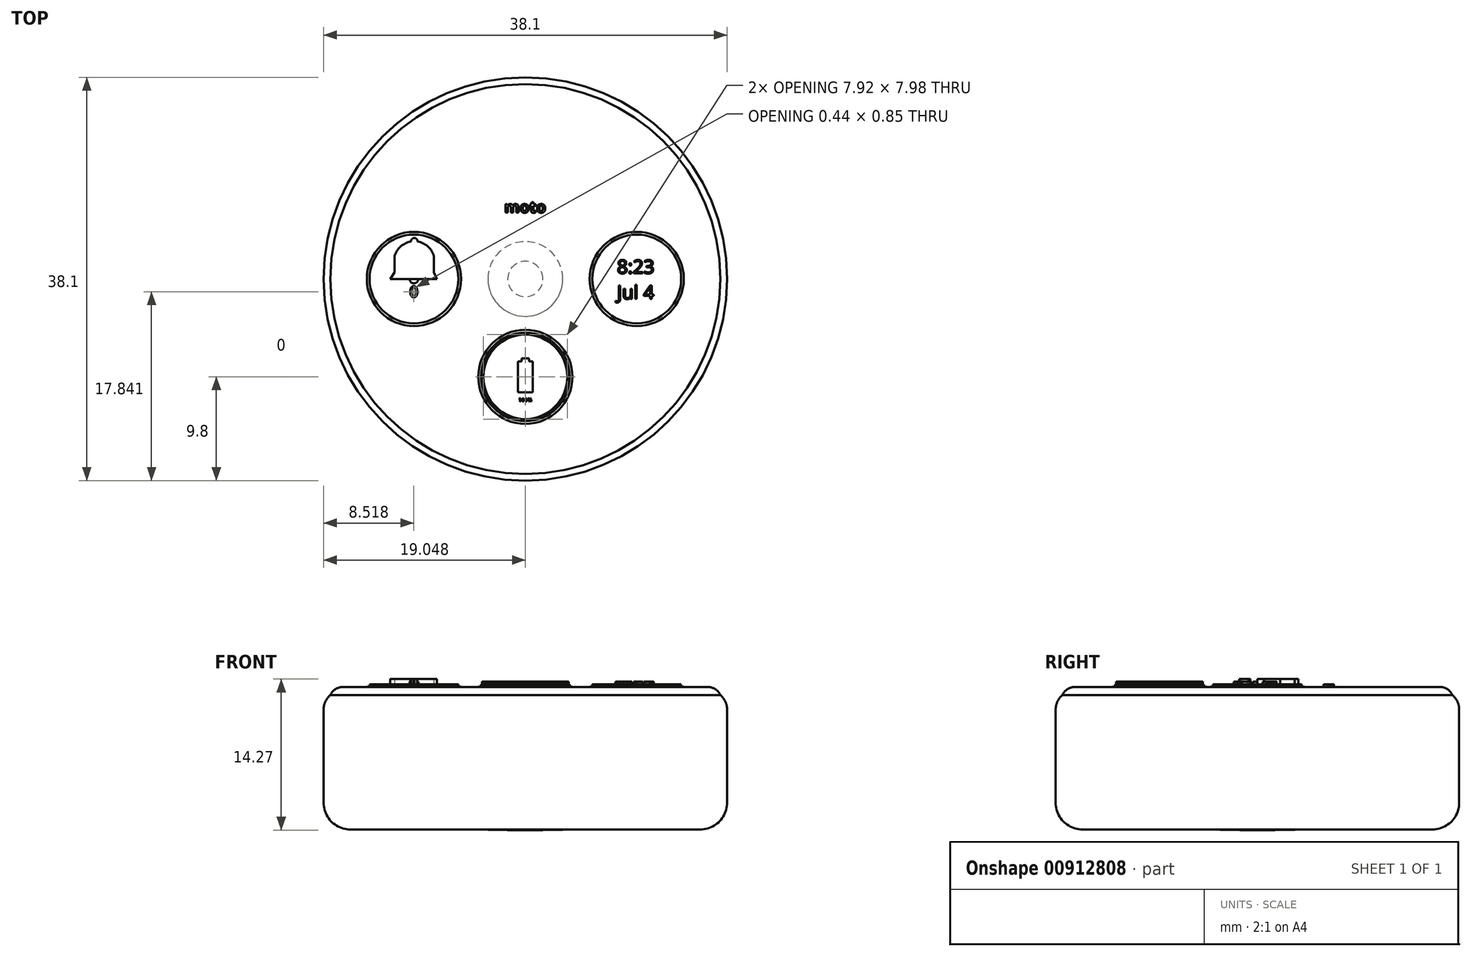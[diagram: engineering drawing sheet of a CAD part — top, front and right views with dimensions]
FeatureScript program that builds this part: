
annotation { "Feature Type Name" : "Feature", "Feature Type Description" : "" }
export const myFeature = defineFeature(function(context is Context, id is Id, definition is map)
    precondition{}
    {
        {
            var Q0;
            Q0=qCreatedBy(makeId("Top.planeOp"),FACE);
            var sketch = newSketch(context, id + "F0", { "sketchPlane" : qUnion([Q0])});
            skCircle(sketch, "E0", {"center": v(0, 0) * mm, "radius": 19.05 * mm});
            skSolve(sketch);
        }
        {
            var Q0;
            Q0 = qSketchRegion(id + "F0", true);
            extrude(context, id + "F1", {"entities" : qUnion([Q0]), "depth" : 12.7 * mm, "offsetDistance" : 25.4 * mm});
        }
        {
            var Q0;
            Q0=makeQuery(id+"F1.opExtrude","CAP_FACE",FACE,{"disambiguationData":[OSD([sQuery(id+"F0.wireOp",EDGE,"E0")])],"isStart":false});
            var sketch = newSketch(context, id + "F2", { "sketchPlane" : qUnion([Q0])});
            skCircle(sketch, "E1", {"center": v(0, 0) * mm, "radius": 18.41 * mm});
            skSolve(sketch);
        }
        {
            var Q0;
            Q0 = qSketchRegion(id + "F2", true);
            extrude(context, id + "F3", {"entities" : qUnion([Q0]), "operationType" : NewBodyOperationType.ADD, "depth" : 0.76 * mm, "offsetDistance" : 25.4 * mm});
        }
        {
            var Q0;
            Q0=makeQuery(id+"F3.opExtrude","CAP_EDGE",EDGE,{"disambiguationData":[OSD([sQuery(id+"F2.wireOp",EDGE,"E1")])],"isStart":false});
            fillet(context, id + "F4", {"entities" : qUnion([Q0]), "radius" : 1.27 * mm, "tangentPropagation" : true, "allowEdgeOverflow" : false});
        }
        {
            var Q0;
            Q0=makeQuery(id+"F1.opExtrude","CAP_EDGE",EDGE,{"disambiguationData":[OSD([sQuery(id+"F0.wireOp",EDGE,"E0")])],"isStart":false});
            fillet(context, id + "F5", {"entities" : qUnion([Q0]), "radius" : 1.78 * mm, "tangentPropagation" : true, "allowEdgeOverflow" : false});
        }
        {
            var Q0;
            Q0=makeQuery(id+"F1.opExtrude","CAP_EDGE",EDGE,{"disambiguationData":[OSD([sQuery(id+"F0.wireOp",EDGE,"E0")])],"isStart":true});
            fillet(context, id + "F6", {"entities" : qUnion([Q0]), "radius" : 2.54 * mm, "tangentPropagation" : true, "allowEdgeOverflow" : false});
        }
        {
            var Q0;
            Q0=makeQuery(id+"F1.opExtrude","CAP_FACE",FACE,{"disambiguationData":[OSD([sQuery(id+"F0.wireOp",EDGE,"E0")])],"isStart":true});
            var sketch = newSketch(context, id + "F7", { "sketchPlane" : qUnion([Q0])});
            skCircle(sketch, "E2", {"center": v(0, 0) * mm, "radius": 3.53 * mm});
            skCircle(sketch, "E3", {"center": v(0, 0) * mm, "radius": 1.66 * mm});
            skSolve(sketch);
        }
        {
            var Q0;
            Q0 = qSketchRegion(id + "F7", true);
            extrude(context, id + "F8", {"entities" : qUnion([Q0]), "operationType" : NewBodyOperationType.ADD, "depth" : 0.03 * mm, "offsetDistance" : 25.4 * mm});
        }
        {
            var Q0;
            Q0=makeQuery(id+"F8.boolean.opBoolean","SPLIT",FACE,{"disambiguationData":[TD([makeQuery(id+"F8.opExtrude","SWEPT_FACE",FACE,{"disambiguationData":[OSD([sQuery(id+"F7.wireOp",EDGE,"E3")])]})])],"derivedFrom":makeQuery(id+"F1.opExtrude","CAP_FACE",FACE,{"disambiguationData":[OSD([sQuery(id+"F0.wireOp",EDGE,"E0")])],"isStart":true})});
            extrude(context, id + "F9", {"entities" : qUnion([Q0]), "operationType" : NewBodyOperationType.ADD, "depth" : 0.05 * mm, "offsetDistance" : 25.4 * mm});
        }
        {
            var Q0;
            Q0=makeQuery(id+"F3.opExtrude","CAP_FACE",FACE,{"disambiguationData":[OSD([sQuery(id+"F2.wireOp",EDGE,"E1")])],"isStart":false});
            var sketch = newSketch(context, id + "F10", { "sketchPlane" : qUnion([Q0])});
            skText(sketch, "E4", { "text": "moto", "fontName": "OpenSans-Bold.ttf"});
            skCircle(sketch, "E5", {"center": v(0, -9.25) * mm, "radius": 4.2 * mm});
            skCircle(sketch, "E6", {"center": v(10.52, 0) * mm, "radius": 4.2 * mm});
            skCircle(sketch, "E7", {"center": v(-10.52, 0) * mm, "radius": 4.2 * mm});
            const initialGuessF10  = {"E4": [-0.00199, 0.00626, 1, 0, 0.00107]};
            skSetInitialGuess(sketch, initialGuessF10);
            skSolve(sketch);
        }
        {
            var Q0;
            Q0 = qSketchRegion(id + "F10", true);
            extrude(context, id + "F11", {"entities" : qUnion([Q0]), "operationType" : NewBodyOperationType.ADD, "depth" : 0.25 * mm, "offsetDistance" : 25.4 * mm});
        }
        {
            var Q0;
            {var subQ0=sQuery(id+"F2.wireOp",EDGE,"E1");Q0=makeQuery(id+"F11.boolean.opBoolean","SPLIT",FACE,{"disambiguationData":[TD([makeQuery(id+"F4.opFillet","BLEND_FACE",FACE,{"disambiguationData":[OSD([subQ0])]})])],"derivedFrom":makeQuery(id+"F3.opExtrude","CAP_FACE",FACE,{"disambiguationData":[OSD([subQ0])],"isStart":false})});}
            var sketch = newSketch(context, id + "F12", { "sketchPlane" : qUnion([Q0])});
            skCircle(sketch, "E8", {"center": v(-10.52, 0) * mm, "radius": 4.45 * mm});
            skCircle(sketch, "E9", {"center": v(0, -9.25) * mm, "radius": 4.45 * mm});
            skCircle(sketch, "E10", {"center": v(10.52, 0) * mm, "radius": 4.45 * mm});
            skSolve(sketch);
        }
        {
            var Q0;
            Q0 = qSketchRegion(id + "F12", true);
            extrude(context, id + "F13", {"entities" : qUnion([Q0]), "operationType" : NewBodyOperationType.ADD, "depth" : 0.03 * mm, "offsetDistance" : 25.4 * mm});
        }
        {
            var Q0;
            Q0=makeQuery(id+"F11.opExtrude","CAP_FACE",FACE,{"disambiguationData":[OSD([sQuery(id+"F10.wireOp",EDGE,"E5")])],"isStart":false});
            var sketch = newSketch(context, id + "F14", { "sketchPlane" : qUnion([Q0])});
            skLineSegment(sketch, "E11.top", {"start": v(-0.69, -10.72) * mm, "end": v(0.69, -10.72) * mm});
            skLineSegment(sketch, "E11.left", {"start": v(-0.69, -7.78) * mm, "end": v(-0.69, -10.72) * mm});
            skLineSegment(sketch, "E11.right", {"start": v(0.69, -7.78) * mm, "end": v(0.69, -10.72) * mm});
            skPoint(sketch, "E11.middle", {"position": v(0, -9.25) * mm});
            skLineSegment(sketch, "E12.bottom", {"start": v(-0.35, -7.52) * mm, "end": v(0.35, -7.52) * mm});
            skPoint(sketch, "E12.middle", {"position": v(0, -7.78) * mm});
            skLineSegment(sketch, "E13", {"start": v(-0.35, -7.52) * mm, "end": v(-0.35, -7.78) * mm});
            skLineSegment(sketch, "E14", {"start": v(0.35, -7.52) * mm, "end": v(0.35, -7.78) * mm});
            skLineSegment(sketch, "E15", {"start": v(-0.69, -7.78) * mm, "end": v(-0.35, -7.78) * mm});
            skLineSegment(sketch, "E16", {"start": v(0.69, -7.78) * mm, "end": v(0.35, -7.78) * mm});
            skPoint(sketch, "E17.startSnap0", {"position": v(0, -7.52) * mm});
            skPoint(sketch, "E17.endSnap0", {"position": v(0, -7.52) * mm});
            skPoint(sketch, "E18", {"position": v(0, -5.26) * mm});
            skPoint(sketch, "E19", {"position": v(0, -13.24) * mm});
            skArc(sketch, "E20", {"start": v(0, -13.24) * mm, "mid": v(3.96, -9.25) * mm, "end": v(0, -5.26) * mm});
            skArc(sketch, "E21", {"start": v(0, -5.26) * mm, "mid": v(-3.96, -9.25) * mm, "end": v(0, -13.24) * mm});
            skPoint(sketch, "E22", {"position": v(0, -5.16) * mm});
            skPoint(sketch, "E23", {"position": v(0, -13.34) * mm});
            skArc(sketch, "E24", {"start": v(0, -13.34) * mm, "mid": v(4.09, -9.25) * mm, "end": v(0, -5.16) * mm});
            skArc(sketch, "E25", {"start": v(0, -5.16) * mm, "mid": v(-4.08, -9.25) * mm, "end": v(0, -13.34) * mm});
            skText(sketch, "E26", { "text": "100%\n", "fontName": "OpenSans-Regular.ttf"});
            const initialGuessF14  = {"E26": [-0.00064, -0.0116, 1, 0, 0.00036]};
            skSetInitialGuess(sketch, initialGuessF14);
            skSolve(sketch);
        }
        {
            var Q0;
            {var subQ4=sQuery(id+"F14.wireOp",EDGE,"E11.left");Q0=makeQuery(id+"F14.imprint","IMPRINT",FACE,{"disambiguationData":[TD([[makeQuery(id+"F14.imprint","IMPRINT",EDGE,{"derivedFrom":subQ4}),1.0]])]});}
            var Q1;
            {var subQ4=sQuery(id+"F14.wireOp",EDGE,"E11.right");Q1=makeQuery(id+"F14.imprint","IMPRINT",FACE,{"disambiguationData":[TD([[makeQuery(id+"F14.imprint","IMPRINT",EDGE,{"derivedFrom":subQ4}),-1.0]])]});}
            extrude(context, id + "F15", {"entities" : qUnion([Q0, Q1]), "depth" : 0.03 * mm, "offsetDistance" : 25.4 * mm});
        }
        {
            var Q0;
            {var subQ0=sQuery(id+"F14.wireOp",EDGE,"E21");Q0=makeQuery(id+"F14.imprint","IMPRINT",FACE,{"disambiguationData":[TD([[makeQuery(id+"F14.imprint","IMPRINT",EDGE,{"derivedFrom":subQ0}),-1.0]])]});}
            var Q1;
            {var subQ1=sQuery(id+"F14.wireOp",EDGE,"E20");Q1=makeQuery(id+"F14.imprint","IMPRINT",FACE,{"disambiguationData":[TD([[makeQuery(id+"F14.imprint","IMPRINT",EDGE,{"derivedFrom":subQ1}),-1.0]])]});}
            var Q2;
            Q2=sQuery(id+"F14.wireOp",EDGE,"E25");
            var Q3;
            Q3=sQuery(id+"F14.wireOp",EDGE,"E24");
            extrude(context, id + "F16", {"entities" : qUnion([Q0, Q1]), "surfaceEntities" : qUnion([Q2, Q3]), "depth" : 0.03 * mm, "offsetDistance" : 25.4 * mm});
        }
        {
            var Q0;
            Q0 = qSketchRegion(id + "F14", true);
            extrude(context, id + "F17", {"entities" : qUnion([Q0]), "depth" : 0.25 * mm, "offsetDistance" : 25.4 * mm});
        }
        {
            var Q0;
            Q0=makeQuery(id+"F14.imprint","IMPRINT",FACE,{"disambiguationData":[TD([[makeQuery(id+"F14.imprint","IMPRINT",EDGE,{"derivedFrom":sQuery(id+"F14.wireOp",EDGE,"E26.sketch_text.stroke-33")}),1.0]])]});
            var Q1;
            Q1=makeQuery(id+"F14.imprint","IMPRINT",FACE,{"disambiguationData":[TD([[makeQuery(id+"F14.imprint","IMPRINT",EDGE,{"derivedFrom":sQuery(id+"F14.wireOp",EDGE,"E26.sketch_text.stroke-17")}),1.0]])]});
            var Q2;
            Q2=makeQuery(id+"F14.imprint","IMPRINT",FACE,{"disambiguationData":[TD([[makeQuery(id+"F14.imprint","IMPRINT",EDGE,{"derivedFrom":sQuery(id+"F14.wireOp",EDGE,"E26.sketch_text.stroke-0")}),-1.0]])]});
            var Q3;
            Q3=makeQuery(id+"F14.imprint","IMPRINT",FACE,{"disambiguationData":[TD([[makeQuery(id+"F14.imprint","IMPRINT",EDGE,{"derivedFrom":sQuery(id+"F14.wireOp",EDGE,"E26.sketch_text.stroke-41")}),1.0]])]});
            var Q4;
            Q4=makeQuery(id+"F14.imprint","IMPRINT",FACE,{"disambiguationData":[TD([[makeQuery(id+"F14.imprint","IMPRINT",EDGE,{"derivedFrom":sQuery(id+"F14.wireOp",EDGE,"E26.sketch_text.stroke-71")}),-1.0]])]});
            var Q5;
            Q5=makeQuery(id+"F14.imprint","IMPRINT",FACE,{"disambiguationData":[TD([[makeQuery(id+"F14.imprint","IMPRINT",EDGE,{"derivedFrom":sQuery(id+"F14.wireOp",EDGE,"E26.sketch_text.stroke-55")}),1.0]])]});
            extrude(context, id + "F18", {"entities" : qUnion([Q0, Q1, Q2, Q3, Q4, Q5]), "operationType" : NewBodyOperationType.ADD, "depth" : 0.25 * mm, "offsetDistance" : 25.4 * mm});
        }
        {
            var Q0;
            {var subQ0=sQuery(id+"F2.wireOp",EDGE,"E1");Q0=makeQuery(id+"F11.boolean.opBoolean","SPLIT",FACE,{"disambiguationData":[TD([makeQuery(id+"F4.opFillet","BLEND_FACE",FACE,{"disambiguationData":[OSD([subQ0])]})])],"derivedFrom":makeQuery(id+"F3.opExtrude","CAP_FACE",FACE,{"disambiguationData":[OSD([subQ0])],"isStart":false})});}
            var sketch = newSketch(context, id + "F19", { "sketchPlane" : qUnion([Q0])});
            skLineSegment(sketch, "E27.bottom", {"start": v(0, 14.95) * mm, "end": v(0, 14.95) * mm});
            skLineSegment(sketch, "E27.top", {"start": v(0, 0) * mm, "end": v(0, 0) * mm});
            skLineSegment(sketch, "E27.left", {"start": v(0, 14.95) * mm, "end": v(0, 0) * mm});
            skLineSegment(sketch, "E27.right", {"start": v(0, 14.95) * mm, "end": v(0, 0) * mm});
            skPoint(sketch, "E27.middle", {"position": v(0, 7.47) * mm});
            skPoint(sketch, "E28", {"position": v(0, 0) * mm});
            skLineSegment(sketch, "E29", {"start": v(0, 0) * mm, "end": v(4.6, 0) * mm});
            skLineSegment(sketch, "E30", {"start": v(4.6, 0) * mm, "end": v(4.6, 0) * mm});
            skLineSegment(sketch, "E31", {"start": v(4.6, 0) * mm, "end": v(0, 0) * mm});
            skSolve(sketch);
        }
        {
            var Q0;
            Q0=sQuery(id+"F19.wireOp",EDGE,"E27.right");
            var Q1;
            Q1=sQuery(id+"F19.wireOp",EDGE,"E31");
            extrude(context, id + "F20", {"bodyType" : ToolBodyType.SURFACE, "surfaceEntities" : qUnion([Q0, Q1]), "depth" : 0.25 * mm, "offsetDistance" : 25.4 * mm});
        }
        {
            var Q0;
            Q0=makeQuery(id+"F11.opExtrude","CAP_FACE",FACE,{"disambiguationData":[OSD([sQuery(id+"F10.wireOp",EDGE,"E6")])],"isStart":false});
            var sketch = newSketch(context, id + "F21", { "sketchPlane" : qUnion([Q0])});
            skText(sketch, "E32", { "text": "8:23\nJul 4", "fontName": "OpenSans-Regular.ttf"});
            const initialGuessF21  = {"E32": [0.00866, 0.00052, 1, 0, 0.00128]};
            skSetInitialGuess(sketch, initialGuessF21);
            skSolve(sketch);
        }
        {
            var Q0;
            Q0 = qSketchRegion(id + "F21", true);
            extrude(context, id + "F22", {"entities" : qUnion([Q0]), "depth" : 0.25 * mm, "offsetDistance" : 25.4 * mm});
        }
        {
            var Q0;
            Q0=makeQuery(id+"F11.opExtrude","CAP_FACE",FACE,{"disambiguationData":[OSD([sQuery(id+"F10.wireOp",EDGE,"E7")])],"isStart":false});
            var sketch = newSketch(context, id + "F23", { "sketchPlane" : qUnion([Q0])});
            skLineSegment(sketch, "E33", {"start": v(-10.52, 0) * mm, "end": v(-12.75, 0) * mm});
            skLineSegment(sketch, "E34", {"start": v(-10.52, 0) * mm, "end": v(-8.35, 0) * mm});
            skLineSegment(sketch, "E35", {"start": v(-8.35, 0) * mm, "end": v(-8.62, 0.63) * mm});
            skLineSegment(sketch, "E36", {"start": v(-8.62, 0.63) * mm, "end": v(-12.35, 0.63) * mm});
            skLineSegment(sketch, "E37", {"start": v(-12.35, 0.63) * mm, "end": v(-12.75, 0) * mm});
            skLineSegment(sketch, "E38", {"start": v(-12.35, 0.63) * mm, "end": v(-12.35, 2.15) * mm});
            skLineSegment(sketch, "E39", {"start": v(-8.62, 0.63) * mm, "end": v(-8.62, 2.15) * mm});
            skLineSegment(sketch, "E40", {"start": v(-12.35, 2.15) * mm, "end": v(-8.62, 2.15) * mm});
            skArc(sketch, "E41", {"start": v(-8.62, 2.15) * mm, "mid": v(-10.49, 3.56) * mm, "end": v(-12.35, 2.15) * mm});
            skArc(sketch, "E42", {"start": v(-10.18, 3.53) * mm, "mid": v(-10.49, 3.87) * mm, "end": v(-10.8, 3.53) * mm});
            skArc(sketch, "E43", {"start": v(-10.93, 0) * mm, "mid": v(-10.52, -0.41) * mm, "end": v(-10.1, 0) * mm});
            skText(sketch, "E44", { "text": "0\n", "fontName": "OpenSans-Regular.ttf"});
            skLineSegment(sketch, "E45", {"start": v(-10.52, 0) * mm, "end": v(-10.52, -2.48) * mm});
            const initialGuessF23  = {"E44": [-0.01094, -0.00172, 1, 0, 0.00103]};
            skSetInitialGuess(sketch, initialGuessF23);
            skSolve(sketch);
        }
        {
            var Q0;
            {var subQ0=sQuery(id+"F23.wireOp",EDGE,"E35");Q0=makeQuery(id+"F23.imprint","IMPRINT",FACE,{"disambiguationData":[TD([[makeQuery(id+"F23.imprint","IMPRINT",EDGE,{"derivedFrom":subQ0}),1.0]])]});}
            var Q1;
            Q1=makeQuery(id+"F23.imprint","IMPRINT",FACE,{"disambiguationData":[TD([[makeQuery(id+"F23.imprint","IMPRINT",EDGE,{"derivedFrom":sQuery(id+"F23.wireOp",EDGE,"E36")}),-1.0]])]});
            var Q2;
            {var subQ10=sQuery(id+"F23.wireOp",EDGE,"E44.sketch_text.stroke-2");Q2=makeQuery(id+"F23.imprint","IMPRINT",FACE,{"disambiguationData":[TD([[makeQuery(id+"F23.imprint","IMPRINT",EDGE,{"derivedFrom":subQ10}),-1.0]])]});}
            var Q3;
            {var subQ5=sQuery(id+"F23.wireOp",EDGE,"E44.sketch_text.stroke-0");Q3=makeQuery(id+"F23.imprint","IMPRINT",FACE,{"disambiguationData":[TD([[makeQuery(id+"F23.imprint","IMPRINT",EDGE,{"derivedFrom":subQ5}),-1.0]])]});}
            var Q4;
            {var subQ0=sQuery(id+"F23.wireOp",EDGE,"E40");Q4=makeQuery(id+"F23.imprint","IMPRINT",FACE,{"disambiguationData":[TD([[makeQuery(id+"F23.imprint","IMPRINT",EDGE,{"derivedFrom":subQ0}),1.0]])]});}
            var Q5;
            {var subQ0=sQuery(id+"F23.wireOp",EDGE,"E42");Q5=makeQuery(id+"F23.imprint","IMPRINT",FACE,{"disambiguationData":[TD([[makeQuery(id+"F23.imprint","IMPRINT",EDGE,{"derivedFrom":subQ0}),1.0]])]});}
            extrude(context, id + "F24", {"entities" : qUnion([Q0, Q1, Q2, Q3, Q4, Q5]), "depth" : 0.5 * mm, "offsetDistance" : 25.4 * mm});
        }
        {
            var Q0;
            {var subQ1=sQuery(id+"F23.wireOp",EDGE,"E33");var subQ3=sQuery(id+"F23.wireOp",EDGE,"E43");var subQ4=makeQuery(id+"F23.imprint","INTERSECT",VERTEX,{"derivedFrom":[subQ1,subQ3]});Q0=makeQuery(id+"F23.imprint","IMPRINT",FACE,{"disambiguationData":[TD([[makeQuery(id+"F23.imprint","IMPRINT",EDGE,{"disambiguationData":[TD([[subQ4,-1.0]])],"derivedFrom":subQ3}),1.0]])]});}
            var Q1;
            {var subQ1=sQuery(id+"F23.wireOp",EDGE,"E34");var subQ3=sQuery(id+"F23.wireOp",EDGE,"E43");var subQ4=makeQuery(id+"F23.imprint","INTERSECT",VERTEX,{"derivedFrom":[subQ1,subQ3]});Q1=makeQuery(id+"F23.imprint","IMPRINT",FACE,{"disambiguationData":[TD([[makeQuery(id+"F23.imprint","IMPRINT",EDGE,{"disambiguationData":[TD([[subQ4,1.0]])],"derivedFrom":subQ3}),1.0]])]});}
            extrude(context, id + "F25", {"entities" : qUnion([Q0, Q1]), "depth" : 0.25 * mm, "offsetDistance" : 25.4 * mm});
        }
    });
